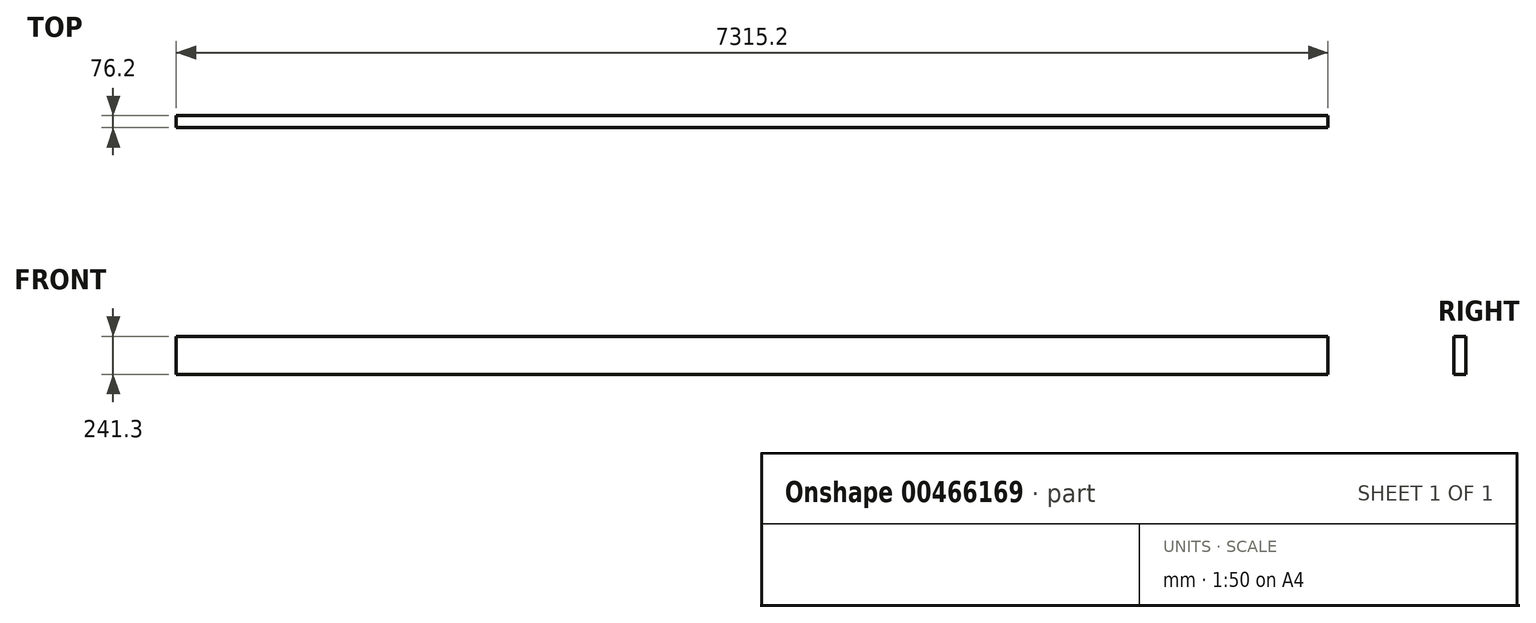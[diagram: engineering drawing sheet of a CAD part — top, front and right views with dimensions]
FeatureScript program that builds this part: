
annotation { "Feature Type Name" : "Feature", "Feature Type Description" : "" }
export const myFeature = defineFeature(function(context is Context, id is Id, definition is map)
    precondition{}
    {
        {
            var Q0;
            Q0=qCreatedBy(makeId("Right.planeOp"),FACE);
            var sketch = newSketch(context, id + "F0", { "sketchPlane" : qUnion([Q0])});
            skLineSegment(sketch, "E0.bottom", {"start": v(26.5, 0) * mm, "end": v(102.7, 0) * mm});
            skLineSegment(sketch, "E0.top", {"start": v(26.5, 241.3) * mm, "end": v(102.7, 241.3) * mm});
            skLineSegment(sketch, "E0.left", {"start": v(26.5, 0) * mm, "end": v(26.5, 241.3) * mm});
            skLineSegment(sketch, "E0.right", {"start": v(102.7, 0) * mm, "end": v(102.7, 241.3) * mm});
            skSolve(sketch);
        }
        {
            var Q0;
            Q0=makeQuery(id+"F0.imprint","IMPRINT",FACE,{"disambiguationData":[TD([[makeQuery(id+"F0.imprint","IMPRINT",EDGE,{"derivedFrom":sQuery(id+"F0.wireOp",EDGE,"E0.bottom")}),1.0]])]});
            extrude(context, id + "F1", {"entities" : qUnion([Q0]), "oppositeDirection" : true, "depth" : 7315.2 * mm});
        }
    });
